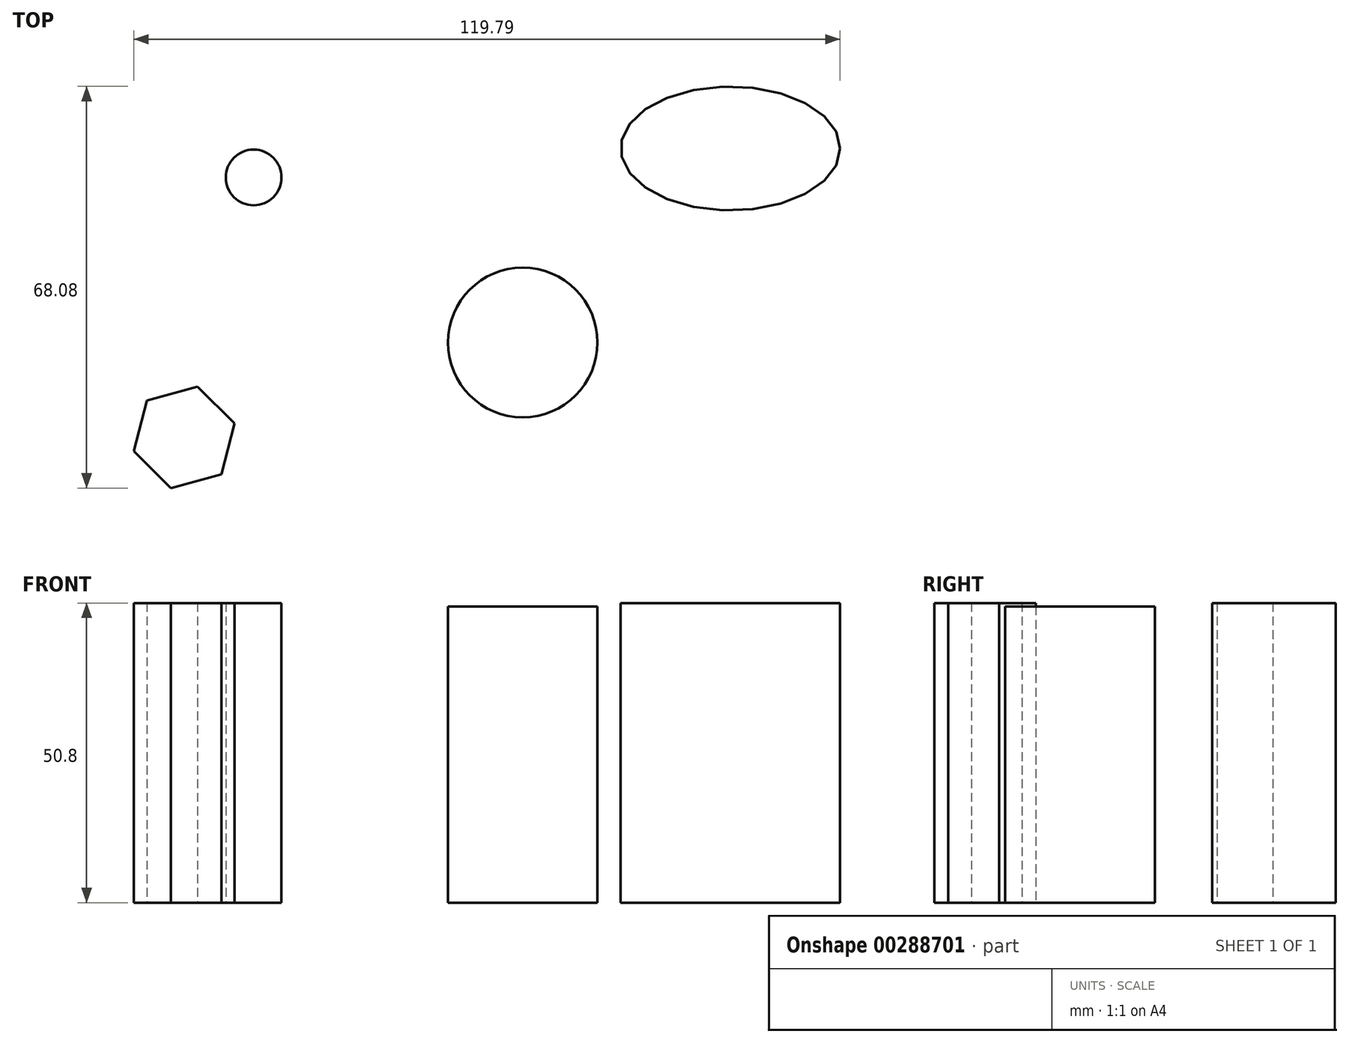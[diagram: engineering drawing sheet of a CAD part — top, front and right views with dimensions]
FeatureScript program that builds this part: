
annotation { "Feature Type Name" : "Feature", "Feature Type Description" : "" }
export const myFeature = defineFeature(function(context is Context, id is Id, definition is map)
    precondition{}
    {
        {
            var Q0;
            Q0=qCreatedBy(makeId("Front.planeOp"),FACE);
            var sketch = newSketch(context, id + "F0", { "sketchPlane" : qUnion([Q0])});
            skLineSegment(sketch, "E0", {"start": v(0, 0) * mm, "end": v(0, 50.22) * mm});
            skLineSegment(sketch, "E1", {"start": v(0, 50.22) * mm, "end": v(12.68, 50.22) * mm});
            skLineSegment(sketch, "E2", {"start": v(12.68, 50.22) * mm, "end": v(12.68, 0) * mm});
            skLineSegment(sketch, "E3", {"start": v(12.68, 0) * mm, "end": v(0, 0) * mm});
            skSolve(sketch);
        }
        {
            var Q0;
            Q0=makeQuery(id+"F0.imprint","IMPRINT",FACE,{"disambiguationData":[TD([[makeQuery(id+"F0.imprint","IMPRINT",EDGE,{"derivedFrom":sQuery(id+"F0.wireOp",EDGE,"E0")}),-1.0]])]});
            var Q1;
            Q1=sQuery(id+"F0.wireOp",EDGE,"E0");
            revolve(context, id + "F1", {"entities" : qUnion([Q0]), "axis" : qUnion([Q1]), "revolveType" : RevolveType.FULL});
        }
        {
            var Q0;
            Q0=qCreatedBy(makeId("Top.planeOp"),FACE);
            var sketch = newSketch(context, id + "F2", { "sketchPlane" : qUnion([Q0])});
            skEllipse(sketch, "E4", {"center": v(35.23, 32.9) * mm, "majorRadius": 18.61 * mm, "minorRadius": 10.5 * mm, "majorAxis": v(1, 0)});
            skCircle(sketch, "E5", {"center": v(-45.63, 27.98) * mm, "radius": 4.73 * mm});
            skCircle(sketch, "E6.cCircle", {"center": v(-57.4, -16.09) * mm, "radius": 8.87 * mm, "construction": true});
            skLineSegment(sketch, "E6.0", {"start": v(-48.84, -13.73) * mm, "end": v(-51.08, -22.32) * mm});
            skLineSegment(sketch, "E6.1", {"start": v(-51.08, -22.32) * mm, "end": v(-59.63, -24.67) * mm});
            skLineSegment(sketch, "E6.2", {"start": v(-59.63, -24.67) * mm, "end": v(-65.95, -18.44) * mm});
            skLineSegment(sketch, "E6.3", {"start": v(-65.95, -18.44) * mm, "end": v(-63.7, -9.85) * mm});
            skLineSegment(sketch, "E6.4", {"start": v(-63.7, -9.85) * mm, "end": v(-55.15, -7.5) * mm});
            skLineSegment(sketch, "E6.5", {"start": v(-55.15, -7.5) * mm, "end": v(-48.84, -13.73) * mm});
            skSolve(sketch);
        }
        {
            var Q0;
            Q0=makeQuery(id+"F2.imprint","IMPRINT",FACE,{"disambiguationData":[TD([[makeQuery(id+"F2.imprint","IMPRINT",EDGE,{"derivedFrom":sQuery(id+"F2.wireOp",EDGE,"E4")}),1.0]])]});
            var Q1;
            Q1=makeQuery(id+"F2.imprint","IMPRINT",FACE,{"disambiguationData":[TD([[makeQuery(id+"F2.imprint","IMPRINT",EDGE,{"derivedFrom":sQuery(id+"F2.wireOp",EDGE,"E5")}),1.0]])]});
            var Q2;
            Q2=makeQuery(id+"F2.imprint","IMPRINT",FACE,{"disambiguationData":[TD([[makeQuery(id+"F2.imprint","IMPRINT",EDGE,{"derivedFrom":sQuery(id+"F2.wireOp",EDGE,"E6.0")}),-1.0]])]});
            extrude(context, id + "F3", {"entities" : qUnion([Q0, Q1, Q2]), "depth" : 50.8 * mm});
        }
    });
